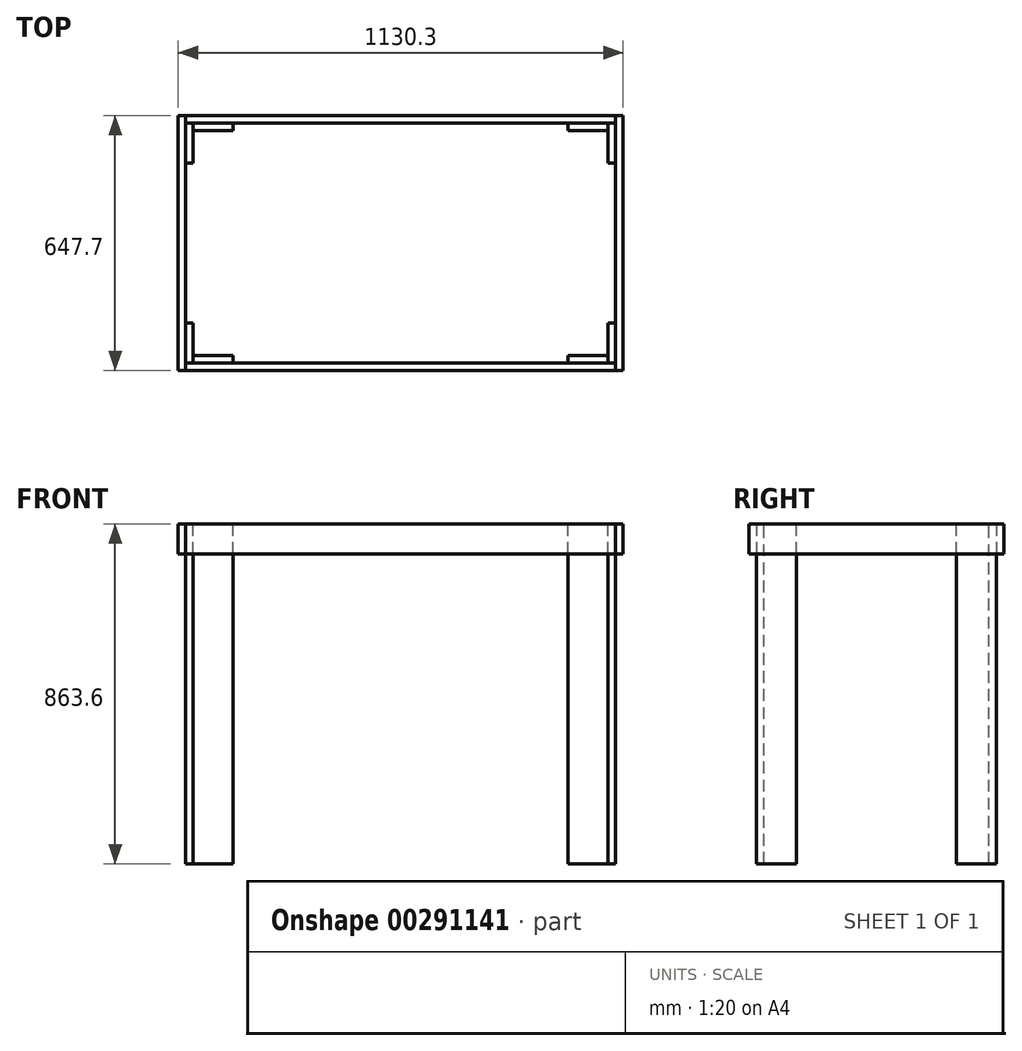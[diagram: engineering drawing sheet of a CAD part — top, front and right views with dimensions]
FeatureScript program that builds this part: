
annotation { "Feature Type Name" : "Feature", "Feature Type Description" : "" }
export const myFeature = defineFeature(function(context is Context, id is Id, definition is map)
    precondition{}
    {
        {
            var Q0;
            Q0=qCreatedBy(makeId("Top.planeOp"),FACE);
            var sketch = newSketch(context, id + "F0", { "sketchPlane" : qUnion([Q0])});
            skLineSegment(sketch, "E0.bottom", {"start": v(0, 0) * mm, "end": v(19.05, 0) * mm});
            skLineSegment(sketch, "E0.top", {"start": v(0, 647.7) * mm, "end": v(19.05, 647.7) * mm});
            skLineSegment(sketch, "E0.left", {"start": v(0, 0) * mm, "end": v(0, 647.7) * mm});
            skLineSegment(sketch, "E0.right", {"start": v(19.05, 0) * mm, "end": v(19.05, 647.7) * mm});
            skSolve(sketch);
        }
        {
            var Q0;
            Q0=makeQuery(id+"F0.imprint","IMPRINT",FACE,{"disambiguationData":[TD([[makeQuery(id+"F0.imprint","IMPRINT",EDGE,{"derivedFrom":sQuery(id+"F0.wireOp",EDGE,"E0.bottom")}),1.0]])]});
            extrude(context, id + "F1", {"entities" : qUnion([Q0]), "depth" : 76.2 * mm});
        }
        {
            var Q0;
            Q0=makeQuery(id+"F1.opExtrude","SWEPT_BODY",BODY,{"disambiguationData":[OSD([sQuery(id+"F0.wireOp",EDGE,"E0.bottom"),sQuery(id+"F0.wireOp",EDGE,"E0.top"),sQuery(id+"F0.wireOp",EDGE,"E0.left"),sQuery(id+"F0.wireOp",EDGE,"E0.right")])]});
            transform(context, id + "F2", {"entities" : qUnion([Q0]), "transformType" : TransformType.TRANSLATION_3D, "dx" : 1111.25 * mm, "dy" : 0 * mm, "dz" : 0 * mm, "makeCopy" : true});
        }
        {
            var Q0;
            Q0=qCreatedBy(makeId("Top.planeOp"),FACE);
            var sketch = newSketch(context, id + "F3", { "sketchPlane" : qUnion([Q0])});
            skLineSegment(sketch, "E1.bottom", {"start": v(19.05, 0) * mm, "end": v(1111.25, 0) * mm});
            skLineSegment(sketch, "E1.top", {"start": v(19.05, 19.05) * mm, "end": v(1111.25, 19.05) * mm});
            skLineSegment(sketch, "E1.left", {"start": v(19.05, 0) * mm, "end": v(19.05, 19.05) * mm});
            skLineSegment(sketch, "E1.right", {"start": v(1111.25, 0) * mm, "end": v(1111.25, 19.05) * mm});
            skSolve(sketch);
        }
        {
            var Q0;
            Q0=makeQuery(id+"F3.imprint","IMPRINT",FACE,{"disambiguationData":[TD([[makeQuery(id+"F3.imprint","IMPRINT",EDGE,{"derivedFrom":sQuery(id+"F3.wireOp",EDGE,"E1.bottom")}),1.0]])]});
            extrude(context, id + "F4", {"entities" : qUnion([Q0]), "depth" : 76.2 * mm});
        }
        {
            var Q0;
            Q0=makeQuery(id+"F4.opExtrude","SWEPT_BODY",BODY,{"disambiguationData":[OSD([sQuery(id+"F3.wireOp",EDGE,"E1.bottom"),sQuery(id+"F3.wireOp",EDGE,"E1.top"),sQuery(id+"F3.wireOp",EDGE,"E1.left"),sQuery(id+"F3.wireOp",EDGE,"E1.right")])]});
            transform(context, id + "F5", {"entities" : qUnion([Q0]), "transformType" : TransformType.TRANSLATION_3D, "dx" : 0 * mm, "dy" : 628.65 * mm, "dz" : 0 * mm, "makeCopy" : true});
        }
        {
            var Q0;
            Q0=qCreatedBy(makeId("Top.planeOp"),FACE);
            var sketch = newSketch(context, id + "F6", { "sketchPlane" : qUnion([Q0])});
            skLineSegment(sketch, "E2.bottom", {"start": v(0, 0) * mm, "end": v(19.05, 0) * mm});
            skLineSegment(sketch, "E2.top", {"start": v(0, 101.6) * mm, "end": v(19.05, 101.6) * mm});
            skLineSegment(sketch, "E2.left", {"start": v(0, 0) * mm, "end": v(0, 101.6) * mm});
            skLineSegment(sketch, "E2.right", {"start": v(19.05, 0) * mm, "end": v(19.05, 101.6) * mm});
            skSolve(sketch);
        }
        {
            var Q0;
            Q0=makeQuery(id+"F6.imprint","IMPRINT",FACE,{"disambiguationData":[TD([[makeQuery(id+"F6.imprint","IMPRINT",EDGE,{"derivedFrom":sQuery(id+"F6.wireOp",EDGE,"E2.bottom")}),1.0]])]});
            extrude(context, id + "F7", {"entities" : qUnion([Q0]), "oppositeDirection" : true, "depth" : 863.6 * mm});
        }
        {
            var Q0;
            Q0=makeQuery(id+"F7.opExtrude","SWEPT_BODY",BODY,{"disambiguationData":[OSD([sQuery(id+"F6.wireOp",EDGE,"E2.bottom"),sQuery(id+"F6.wireOp",EDGE,"E2.top"),sQuery(id+"F6.wireOp",EDGE,"E2.left"),sQuery(id+"F6.wireOp",EDGE,"E2.right")])]});
            transform(context, id + "F8", {"entities" : qUnion([Q0]), "transformType" : TransformType.TRANSLATION_3D, "dx" : 1092.2 * mm, "dy" : 19.05 * mm, "dz" : 76.2 * mm, "makeCopy" : true});
        }
        {
            var Q0;
            Q0=makeQuery(id+"F7.opExtrude","SWEPT_BODY",BODY,{"disambiguationData":[OSD([sQuery(id+"F6.wireOp",EDGE,"E2.bottom"),sQuery(id+"F6.wireOp",EDGE,"E2.top"),sQuery(id+"F6.wireOp",EDGE,"E2.left"),sQuery(id+"F6.wireOp",EDGE,"E2.right")])]});
            transform(context, id + "F9", {"entities" : qUnion([Q0]), "transformType" : TransformType.TRANSLATION_3D, "dx" : 19.05 * mm, "dy" : 19.05 * mm, "dz" : 76.2 * mm, "makeCopy" : false});
        }
        {
            var Q0;
            Q0=makeQuery(id+"F8.opPattern","COPY",BODY,{"derivedFrom":makeQuery(id+"F7.opExtrude","SWEPT_BODY",BODY,{"disambiguationData":[OSD([sQuery(id+"F6.wireOp",EDGE,"E2.bottom"),sQuery(id+"F6.wireOp",EDGE,"E2.top"),sQuery(id+"F6.wireOp",EDGE,"E2.left"),sQuery(id+"F6.wireOp",EDGE,"E2.right")])]}),"instanceName":"1"});
            transform(context, id + "F10", {"entities" : qUnion([Q0]), "transformType" : TransformType.TRANSLATION_3D, "dx" : 0 * mm, "dy" : 508 * mm, "dz" : 0 * mm, "makeCopy" : true});
        }
        {
            var Q0;
            Q0=makeQuery(id+"F7.opExtrude","SWEPT_BODY",BODY,{"disambiguationData":[OSD([sQuery(id+"F6.wireOp",EDGE,"E2.bottom"),sQuery(id+"F6.wireOp",EDGE,"E2.top"),sQuery(id+"F6.wireOp",EDGE,"E2.left"),sQuery(id+"F6.wireOp",EDGE,"E2.right")])]});
            transform(context, id + "F11", {"entities" : qUnion([Q0]), "transformType" : TransformType.TRANSLATION_3D, "dx" : 0 * mm, "dy" : 508 * mm, "dz" : 0 * mm, "makeCopy" : true});
        }
        {
            var Q0;
            Q0=qCreatedBy(makeId("Top.planeOp"),FACE);
            var sketch = newSketch(context, id + "F12", { "sketchPlane" : qUnion([Q0])});
            skLineSegment(sketch, "E3.bottom", {"start": v(0, 0) * mm, "end": v(101.6, 0) * mm});
            skLineSegment(sketch, "E3.top", {"start": v(0, 19.05) * mm, "end": v(101.6, 19.05) * mm});
            skLineSegment(sketch, "E3.left", {"start": v(0, 0) * mm, "end": v(0, 19.05) * mm});
            skLineSegment(sketch, "E3.right", {"start": v(101.6, 0) * mm, "end": v(101.6, 19.05) * mm});
            skSolve(sketch);
        }
        {
            var Q0;
            Q0 = qSketchRegion(id + "F12", true);
            extrude(context, id + "F13", {"entities" : qUnion([Q0]), "oppositeDirection" : true, "depth" : 863.6 * mm});
        }
        {
            var Q0;
            Q0=makeQuery(id+"F13.opExtrude","SWEPT_BODY",BODY,{"disambiguationData":[OSD([sQuery(id+"F12.wireOp",EDGE,"E3.bottom"),sQuery(id+"F12.wireOp",EDGE,"E3.top"),sQuery(id+"F12.wireOp",EDGE,"E3.left"),sQuery(id+"F12.wireOp",EDGE,"E3.right")])]});
            transform(context, id + "F14", {"entities" : qUnion([Q0]), "transformType" : TransformType.TRANSLATION_3D, "dx" : 38.1 * mm, "dy" : 19.05 * mm, "dz" : 76.2 * mm, "makeCopy" : false});
        }
        {
            var Q0;
            Q0=makeQuery(id+"F13.opExtrude","SWEPT_BODY",BODY,{"disambiguationData":[OSD([sQuery(id+"F12.wireOp",EDGE,"E3.bottom"),sQuery(id+"F12.wireOp",EDGE,"E3.top"),sQuery(id+"F12.wireOp",EDGE,"E3.left"),sQuery(id+"F12.wireOp",EDGE,"E3.right")])]});
            transform(context, id + "F15", {"entities" : qUnion([Q0]), "transformType" : TransformType.TRANSLATION_3D, "dx" : 0 * mm, "dy" : 590.55 * mm, "dz" : 0 * mm, "makeCopy" : true});
        }
        {
            var Q0;
            Q0=makeQuery(id+"F13.opExtrude","SWEPT_BODY",BODY,{"disambiguationData":[OSD([sQuery(id+"F12.wireOp",EDGE,"E3.bottom"),sQuery(id+"F12.wireOp",EDGE,"E3.top"),sQuery(id+"F12.wireOp",EDGE,"E3.left"),sQuery(id+"F12.wireOp",EDGE,"E3.right")])]});
            transform(context, id + "F16", {"entities" : qUnion([Q0]), "transformType" : TransformType.TRANSLATION_3D, "dx" : 952.5 * mm, "dy" : 0 * mm, "dz" : 0 * mm, "makeCopy" : true});
        }
        {
            var Q0;
            Q0=makeQuery(id+"F15.opPattern","COPY",BODY,{"derivedFrom":makeQuery(id+"F13.opExtrude","SWEPT_BODY",BODY,{"disambiguationData":[OSD([sQuery(id+"F12.wireOp",EDGE,"E3.bottom"),sQuery(id+"F12.wireOp",EDGE,"E3.top"),sQuery(id+"F12.wireOp",EDGE,"E3.left"),sQuery(id+"F12.wireOp",EDGE,"E3.right")])]}),"instanceName":"1"});
            transform(context, id + "F17", {"entities" : qUnion([Q0]), "transformType" : TransformType.TRANSLATION_3D, "dx" : 0 * mm, "dy" : 0 * mm, "dz" : 0 * mm, "makeCopy" : true});
        }
        {
            var Q0;
            Q0=makeQuery(id+"F16.opPattern","COPY",BODY,{"derivedFrom":makeQuery(id+"F13.opExtrude","SWEPT_BODY",BODY,{"disambiguationData":[OSD([sQuery(id+"F12.wireOp",EDGE,"E3.bottom"),sQuery(id+"F12.wireOp",EDGE,"E3.top"),sQuery(id+"F12.wireOp",EDGE,"E3.left"),sQuery(id+"F12.wireOp",EDGE,"E3.right")])]}),"instanceName":"1"});
            transform(context, id + "F18", {"entities" : qUnion([Q0]), "transformType" : TransformType.TRANSLATION_3D, "dx" : 0 * mm, "dy" : 590.55 * mm, "dz" : 0 * mm, "makeCopy" : true});
        }
    });
